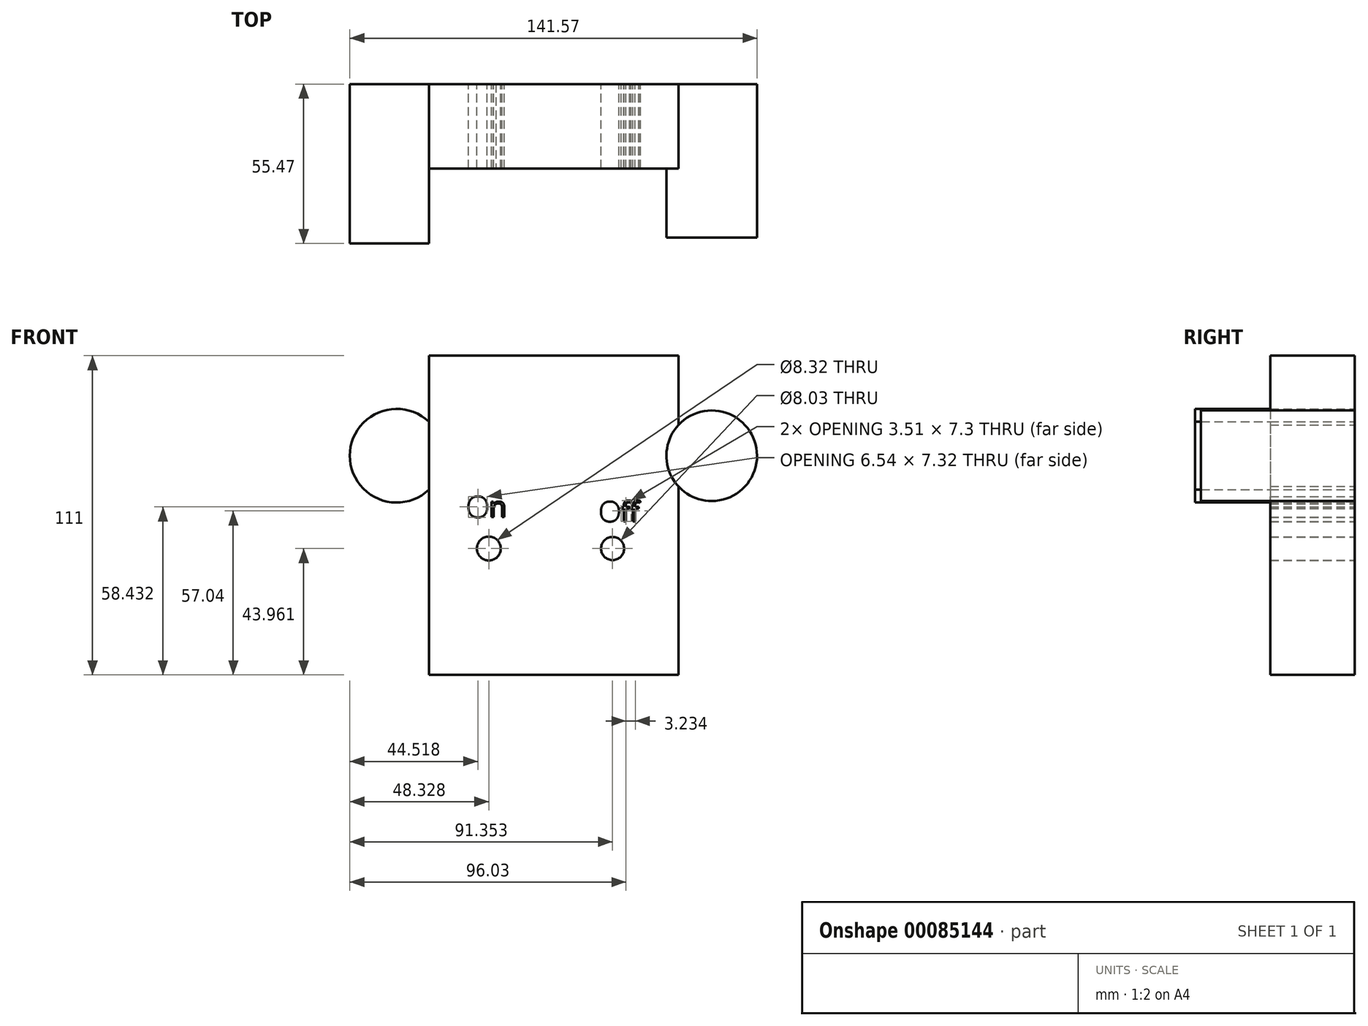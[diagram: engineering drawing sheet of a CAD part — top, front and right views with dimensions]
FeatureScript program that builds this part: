
annotation { "Feature Type Name" : "Feature", "Feature Type Description" : "" }
export const myFeature = defineFeature(function(context is Context, id is Id, definition is map)
    precondition{}
    {
        {
            var Q0;
            Q0=qCreatedBy(makeId("Front.planeOp"),FACE);
            var sketch = newSketch(context, id + "F0", { "sketchPlane" : qUnion([Q0])});
            skLineSegment(sketch, "E0.bottom", {"start": v(-49.26, 34.77) * mm, "end": v(37.42, 34.77) * mm});
            skLineSegment(sketch, "E0.top", {"start": v(-49.26, -76.23) * mm, "end": v(37.42, -76.23) * mm});
            skLineSegment(sketch, "E0.left", {"start": v(-49.26, 34.77) * mm, "end": v(-49.26, -76.23) * mm});
            skLineSegment(sketch, "E0.right", {"start": v(37.42, 34.77) * mm, "end": v(37.42, -76.23) * mm});
            skText(sketch, "E1", { "text": "On", "fontName": "OpenSans-Regular.ttf"});
            skCircle(sketch, "E2", {"center": v(-28.48, -32.27) * mm, "radius": 4.16 * mm});
            skCircle(sketch, "E3", {"center": v(14.54, -32.27) * mm, "radius": 4.01 * mm});
            skText(sketch, "E4", { "text": "Off", "fontName": "OpenSans-Regular.ttf"});
            const initialGuessF0  = {"E1": [-0.03617, -0.02136, 1, 0, 0.00717], "E4": [0.0099, -0.02284, 1, 0, 0.00687]};
            skSetInitialGuess(sketch, initialGuessF0);
            skSolve(sketch);
        }
        {
            var Q0;
            Q0=makeQuery(id+"F0.imprint","IMPRINT",FACE,{"disambiguationData":[TD([[makeQuery(id+"F0.imprint","IMPRINT",EDGE,{"derivedFrom":sQuery(id+"F0.wireOp",EDGE,"E0.bottom")}),-1.0]])]});
            extrude(context, id + "F1", {"entities" : qUnion([Q0]), "depth" : 29.4 * mm});
        }
        {
            var Q0;
            Q0=qCreatedBy(makeId("Front.planeOp"),FACE);
            var sketch = newSketch(context, id + "F2", { "sketchPlane" : qUnion([Q0])});
            skCircle(sketch, "E5", {"center": v(56.3, 0) * mm, "radius": 18.55 * mm});
            skCircle(sketch, "E6", {"center": v(-60.52, 0) * mm, "radius": 16.3 * mm});
            skSolve(sketch);
        }
        {
            var Q0;
            Q0=makeQuery(id+"F2.imprint","IMPRINT",FACE,{"disambiguationData":[TD([[makeQuery(id+"F2.imprint","IMPRINT",EDGE,{"derivedFrom":sQuery(id+"F2.wireOp",EDGE,"E6")}),1.0]])]});
            var Q1;
            Q1=makeQuery(id+"F2.imprint","IMPRINT",FACE,{"disambiguationData":[TD([[makeQuery(id+"F2.imprint","IMPRINT",EDGE,{"derivedFrom":sQuery(id+"F2.wireOp",EDGE,"E5")}),1.0]])]});
            extrude(context, id + "F3", {"entities" : qUnion([Q0, Q1]), "operationType" : NewBodyOperationType.ADD, "depth" : 25.4 * mm});
        }
        {
            var Q0;
            Q0=makeQuery(id+"F3.opExtrude","CAP_FACE",FACE,{"disambiguationData":[OSD([sQuery(id+"F2.wireOp",EDGE,"E6")])],"isStart":false});
            extrude(context, id + "F4", {"entities" : qUnion([Q0]), "operationType" : NewBodyOperationType.ADD, "depth" : 30.07 * mm});
        }
        {
            var Q0;
            Q0=makeQuery(id+"F3.opExtrude","SWEPT_BODY",BODY,{"disambiguationData":[OSD([sQuery(id+"F2.wireOp",EDGE,"E5")])]});
            deleteBodies(context, id + "F5", {"entities" : qUnion([Q0])});
        }
        {
            var Q0;
            Q0=qCreatedBy(makeId("Front.planeOp"),FACE);
            var sketch = newSketch(context, id + "F6", { "sketchPlane" : qUnion([Q0])});
            skCircle(sketch, "E7", {"center": v(49.02, 0) * mm, "radius": 15.75 * mm});
            skSolve(sketch);
        }
        {
            var Q0;
            Q0=makeQuery(id+"F6.imprint","IMPRINT",FACE,{"disambiguationData":[TD([[makeQuery(id+"F6.imprint","IMPRINT",EDGE,{"derivedFrom":sQuery(id+"F6.wireOp",EDGE,"E7")}),1.0]])]});
            extrude(context, id + "F7", {"entities" : qUnion([Q0]), "operationType" : NewBodyOperationType.ADD, "depth" : 53.42 * mm});
        }
    });
